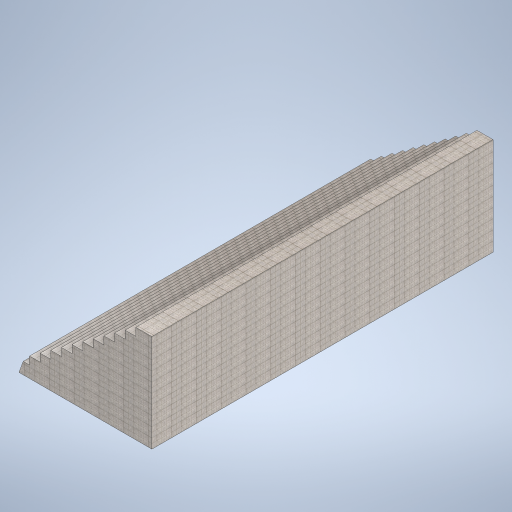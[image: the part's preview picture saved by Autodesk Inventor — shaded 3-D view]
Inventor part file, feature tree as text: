
AUTODESK INVENTOR PART (.ipt)
format: ipt  version: 2024.2 (Build 282272000, 272)  size: 444,416 bytes
history: native  units: mm
features: extrude x3, sketch x3
ambient origin geometry x8: Origin, YZ Plane, XZ Plane, XY Plane, X Axis, Y Axis, Z Axis, Center Point
bodies: Solid1 (feature_tree)
feature tree (6):
  extrude  "Extrusion1"  Depth=7000.0mm
  extrude  "Extrusion2"  Depth=2000.0mm
  extrude  "Extrusion3"  Depth=160.0mm
  sketch  "Sketch1"  dims[d0=2000.0mm d1=7000.0mm]
  sketch  "Sketch2"  dims[d2=2000.0mm d3=0.0mm d4=19.198622mm]
  sketch  "Sketch3"  dims[d5=7000.0mm d6=0.0mm d7=160.0mm d8=160.0mm d9=160.0mm d10=160.0mm d11=160.0mm d12=160.0mm d13=160.0mm d14=160.0mm d15=160.0mm d16=160.0mm d17=160.0mm d18=160.0mm d19=218.0mm d20=218.0mm d21=218.0mm d22=218.0mm d23=218.0mm d24=218.0mm d25=218.0mm d26=218.0mm d27=218.0mm d28=218.0mm d29=218.0mm d30=218.0mm d31=0.0mm d32=0.0mm]
